# Revit family: UA
name_source: partatom
category: Generic Models
units: mm (PartAtom-declared; Revit-internal decimal feet)

## family parameters
Can host rebar = No
Cut with Voids When Loaded = No
Host = Face
Maintain Annotation Orientation = No
Part Type = Normal
Room Calculation Point = No
Round Connector Dimension = Use Diameter
Shared = No

## types (31) — shared parameters
Default Elevation = 4' - 0"
Description = UNIVERSAL ACCESS DOOR
Manufacturer = MIFAB
Material = <By Category>
Model = UA
URL = WWW.MIFAB.COM

## per-type parameters (varying)
| type | Height | Width |
| UA-6"x6" | 0' - 6" | 0' - 6" |
| UA-8"x8" | 0' - 8" | 0' - 8" |
| UA-10"x10" | 0' - 10" | 0' - 10" |
| UA-12"x12" | 1' - 0" | 1' - 0" |
| UA-12"x16" | 1' - 4" | 1' - 0" |
| UA-12"x18" | 1' - 6" | 1' - 0" |
| UA-12"x24" | 2' - 0" | 1' - 0" |
| UA-14” x 14” | 1' - 2" | 1' - 2" |
| UA-14” x 20” | 1' - 8" | 1' - 2" |
| UA-14” x 24” | 2' - 0" | 1' - 2" |
| UA-15” x 15” | 1' - 3" | 1' - 3" |
| UA-16” x 16” | 1' - 4" | 1' - 4" |
| UA-16” x 20” | 1' - 8" | 1' - 4" |
| UA-16” x 24” | 2' - 0" | 1' - 4" |
| UA-18” x 18” | 1' - 6" | 1' - 6" |
| UA-18” x 24” | 2' - 0" | 1' - 6" |
| UA-18” x 36” | 3' - 0" | 1' - 6" |
| UA-20” x 20” | 1' - 8" | 1' - 8" |
| UA-20” x 24” | 2' - 0" | 1' - 8" |
| UA-20” x 30” | 2' - 6" | 1' - 8" |
| UA-22” x 22” | 1' - 10" | 1' - 10" |
| UA-22” x 30” | 2' - 6" | 1' - 10" |
| UA-24” x 24” | 2' - 0" | 2' - 0" |
| UA-24” x 30” | 2' - 6" | 2' - 0" |
| UA-24” x 36” | 3' - 0" | 2' - 0" |
| UA-24” x 48” | 4' - 0" | 2' - 0" |
| UA-30” x 30” | 2' - 6" | 2' - 6" |
| UA-32” x 32” | 2' - 8" | 2' - 8" |
| UA-36” x 36” | 3' - 0" | 3' - 0" |
| UA-36” x 48” | 4' - 0" | 3' - 0" |
| UA-48” x 48” | 4' - 0" | 4' - 0" |

## geometry (parser evidence)
native form markers: Sweep x7
no freeform markers — native parametric forms only
